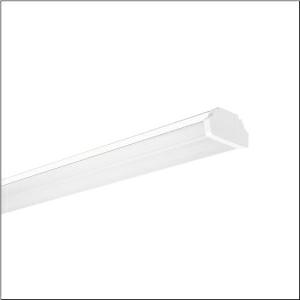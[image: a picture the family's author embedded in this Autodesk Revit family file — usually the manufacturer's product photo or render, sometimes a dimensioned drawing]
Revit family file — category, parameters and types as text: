
# Revit family: dus_r__31_gen_2_53bd812mv4a5c2_5567
name_source: partatom
category: Lighting Fixtures
units: mm (PartAtom-declared; Revit-internal decimal feet)

## family parameters
Cut with Voids When Loaded = No
Host = Face
Light Source = No
Part Type = Normal
Room Calculation Point = No
Round Connector Dimension = Use Diameter
Shared = No

## types (1)
- --- (1 x LED, 10960 lm, 60.5 W, 4000K)
    Apparent Load = 61 VA
    CIE Flux Codes = 47 80 95 93 100
    Color Rendering = 80
    Color Temperature = 4000K
    Default Elevation = 1800 mm
    Description = DUS® 31 Gen.2, luminaire insert, of sheet steel, coil coated, white, length: 1.535mm, width: 81mm, height: 90mm, 5x system unit, system units: 307mm, LED rated luminous flux: 10.960lm, light colour: 840, control gear: ON/OFF Multilumen, control gear: ECG, with plug, 3-pole, with phase selection, mains connection: 220..240V, AC, 50/60Hz, rated input power: 61W, through-wiring accessed according to module size, primary optical cover: cover, of PMMA, light emission: direct distribution, primary light characteristic: symmetric, protection rating (complete): IP20, protection rating (LED compartment): IP50, insulation class (complete): insulation class I (protective earthing), certification: CE, ENEC, VDE, UKCA, impact resistance: IK03, permissible ambient temperature for indoor applications: -35..+40°C, corresponds to IFS (International Featured Standards) requirements for safety and quality in the food industry, reducing of maximum allowable ambient temperature of 5°C with ceiling mounting, packaging unit: 1 piece
    Height = 95 mm
    Lamp = 1 x LED
    Lamp Light Flux = 10960 lm
    Lamp Power = 60.5 W
    Lamp count = 1
    Length = 1535 mm
    Luminous efficacy = 181 lm/W
    Manufacturer = Siteco
    ModVariant = No
    Model = 53BD812MV4A5C2
    Mounting Place = Ceiling
    Mounting Type = Pendant
    Number of Poles = 1
    OnlyDefault = Yes
    Power Factor = 1
    Product Name = DUS® 31 Gen.2
    Product group = luminaire insert
    ProductGroupID = 901
    Protection Class = Protection class I
    Protection Degree = IP 20
    RLX_Detail_Level = 1
    RLX_Emergency_Light_Flux = 0 lm
    RLX_Emergency_Type = 0
    RLX_Emergency_Type_DB = No
    RlxData = <blob elided: 29737 chars, md5=c03d276b>
    Socket = socket
    Standby Power = 0 W
    System Light Flux = 10960 lm
    System Power = 61 W
    Type Comments = factory setting: luminous flux: 100 % | (A | C | E) | 140 mA
    Type Image = l_1319596.jpg
    URL = http://relux.com
    VarID = @adj_010069
    Voltage = 0 V
    Weight = 0.00 kg
    Width = 81 mm

## geometry (parser evidence)
native form markers: Blend x4, Sweep x11
no freeform markers — native parametric forms only
